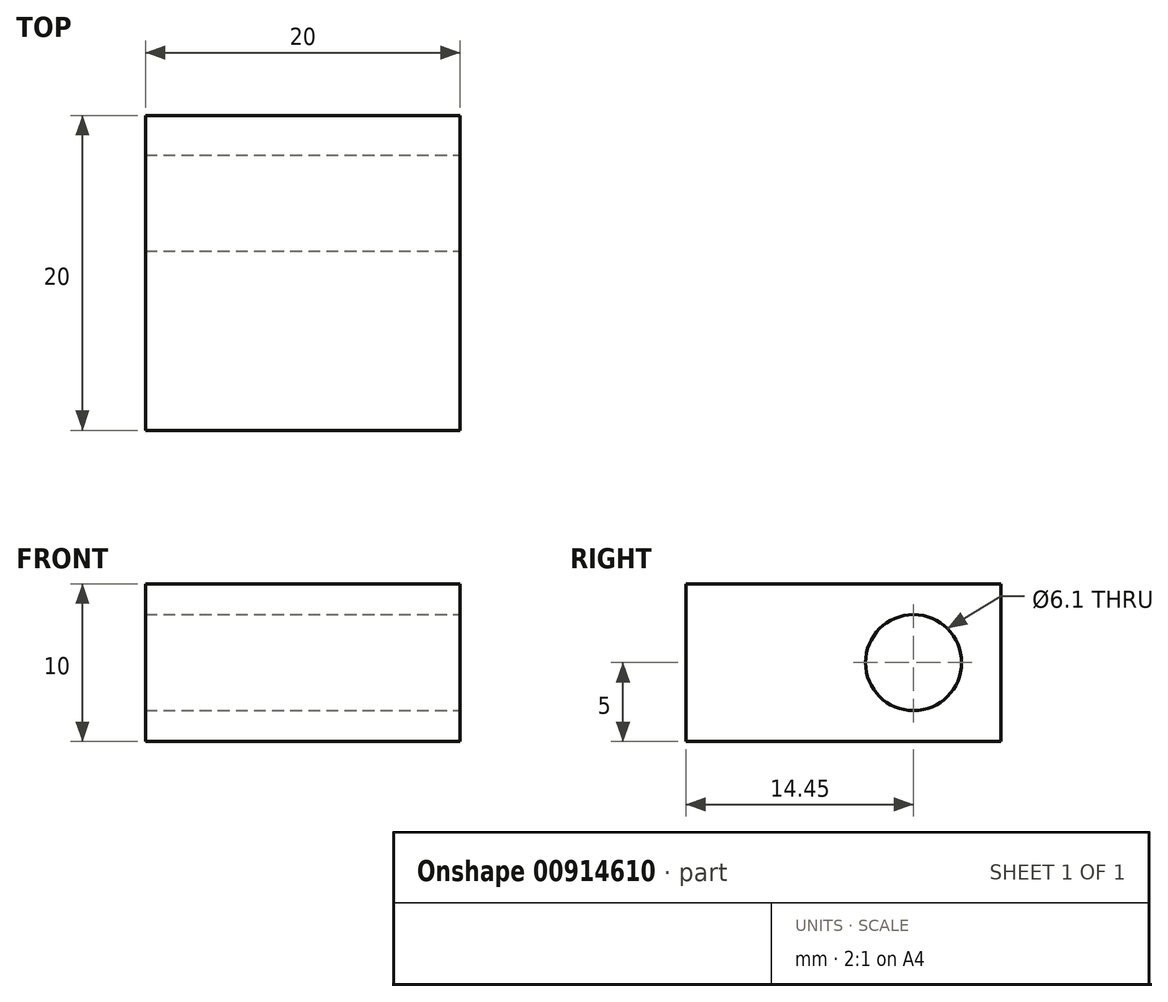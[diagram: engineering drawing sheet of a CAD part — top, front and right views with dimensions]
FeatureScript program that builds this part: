
annotation { "Feature Type Name" : "Feature", "Feature Type Description" : "" }
export const myFeature = defineFeature(function(context is Context, id is Id, definition is map)
    precondition{}
    {
        {
            var Q0;
            Q0=qCreatedBy(makeId("Top.planeOp"),FACE);
            var sketch = newSketch(context, id + "F0", { "sketchPlane" : qUnion([Q0])});
            skLineSegment(sketch, "E0.bottom", {"start": v(-10, -10) * mm, "end": v(10, -10) * mm});
            skLineSegment(sketch, "E0.top", {"start": v(-10, 10) * mm, "end": v(10, 10) * mm});
            skLineSegment(sketch, "E0.left", {"start": v(-10, -10) * mm, "end": v(-10, 10) * mm});
            skLineSegment(sketch, "E0.right", {"start": v(10, -10) * mm, "end": v(10, 10) * mm});
            skLineSegment(sketch, "E1", {"start": v(-10, -10) * mm, "end": v(10, 10) * mm, "construction": true});
            skSolve(sketch);
        }
        {
            var Q0;
            Q0=makeQuery(id+"F0.imprint","IMPRINT",FACE,{"disambiguationData":[TD([[makeQuery(id+"F0.imprint","IMPRINT",EDGE,{"derivedFrom":sQuery(id+"F0.wireOp",EDGE,"E0.bottom")}),1.0]])]});
            extrude(context, id + "F1", {"entities" : qUnion([Q0]), "endBound" : BoundingType.SYMMETRIC, "depth" : 10 * mm, "offsetDistance" : 25.4 * mm});
        }
        {
            var Q0;
            Q0=makeQuery(id+"F1.opExtrude","SWEPT_FACE",FACE,{"disambiguationData":[OSD([sQuery(id+"F0.wireOp",EDGE,"E0.right")])]});
            var sketch = newSketch(context, id + "F2", { "sketchPlane" : qUnion([Q0])});
            skCircle(sketch, "E2", {"center": v(4.45, 0) * mm, "radius": 3.05 * mm});
            skLineSegment(sketch, "E3", {"start": v(4.45, 5) * mm, "end": v(4.45, -5) * mm, "construction": true});
            skSolve(sketch);
        }
        {
            var Q0;
            Q0 = qSketchRegion(id + "F2", true);
            extrude(context, id + "F3", {"entities" : qUnion([Q0]), "operationType" : NewBodyOperationType.REMOVE, "endBound" : BoundingType.THROUGH_ALL, "oppositeDirection" : true, "depth" : 25.4 * mm, "offsetDistance" : 25.4 * mm});
        }
    });
